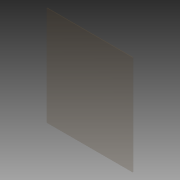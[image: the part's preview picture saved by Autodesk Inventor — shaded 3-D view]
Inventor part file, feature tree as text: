
AUTODESK INVENTOR PART (.ipt)
format: ipt  version: 2012 (Build 160160000, 160)  size: 71,680 bytes
history: native  units: in
note: dims shown in document units (in); Inventor stores cm internally (conversion verified against a paired STEP export)
features: extrude x1, sketch x1
ambient origin geometry x8: Origin, YZ Plane, XZ Plane, XY Plane, X Axis, Y Axis, Z Axis, Center Point
bodies: Solid1 (feature_tree)
feature tree (2):
  extrude  "Extrusion1"  Depth=14.75in
  sketch  "Sketch1"  dims[d0=17.0in d1=14.75in d2=0.125in d3=0.0in]
